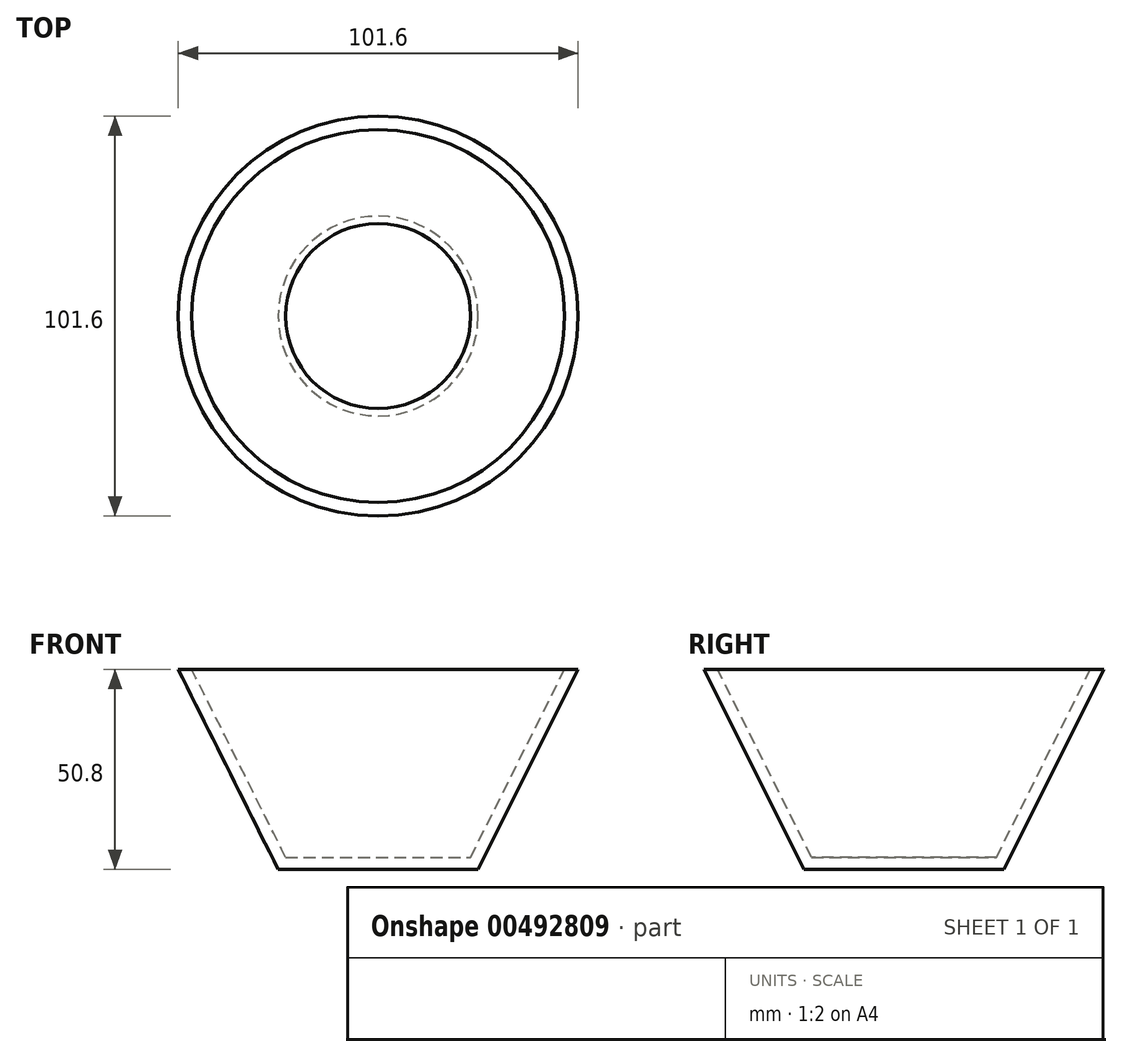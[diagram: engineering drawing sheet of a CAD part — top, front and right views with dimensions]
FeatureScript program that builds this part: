
annotation { "Feature Type Name" : "Feature", "Feature Type Description" : "" }
export const myFeature = defineFeature(function(context is Context, id is Id, definition is map)
    precondition{}
    {
        {
            var Q0;
            Q0=qCreatedBy(makeId("Front.planeOp"),FACE);
            var sketch = newSketch(context, id + "F0", { "sketchPlane" : qUnion([Q0])});
            skLineSegment(sketch, "E0", {"start": v(0, 0) * mm, "end": v(25.4, 0) * mm});
            skLineSegment(sketch, "E1", {"start": v(0, 0) * mm, "end": v(0, 50.8) * mm, "construction": true});
            skLineSegment(sketch, "E2", {"start": v(25.4, 0) * mm, "end": v(50.8, 50.8) * mm});
            skLineSegment(sketch, "E3.0", {"start": v(23.5, 3.07) * mm, "end": v(47.36, 50.8) * mm});
            skLineSegment(sketch, "E3.1", {"start": v(0, 3.07) * mm, "end": v(23.5, 3.07) * mm});
            skLineSegment(sketch, "E4", {"start": v(47.36, 50.8) * mm, "end": v(50.8, 50.8) * mm});
            skLineSegment(sketch, "E5", {"start": v(0, 3.07) * mm, "end": v(0, 0) * mm});
            skSolve(sketch);
        }
        {
            var Q0;
            Q0=makeQuery(id+"F0.imprint","IMPRINT",FACE,{"disambiguationData":[TD([[makeQuery(id+"F0.imprint","IMPRINT",EDGE,{"derivedFrom":sQuery(id+"F0.wireOp",EDGE,"E0")}),1.0]])]});
            var Q1;
            Q1=sQuery(id+"F0.wireOp",EDGE,"E1");
            revolve(context, id + "F1", {"entities" : qUnion([Q0]), "axis" : qUnion([Q1]), "revolveType" : RevolveType.FULL});
        }
    });
